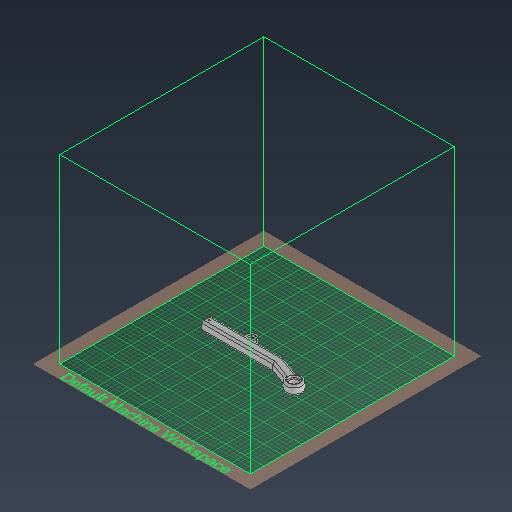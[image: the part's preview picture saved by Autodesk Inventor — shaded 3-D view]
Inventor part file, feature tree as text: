
AUTODESK INVENTOR PART (.ipt)
format: ipt  version: 2021 (Build 250183000, 183)  size: 555,520 bytes
history: native  units: mm
features: extrude x11, sketch x9, fillet x2, shell x1
ambient origin geometry x8: Origin, YZ Plane, XZ Plane, XY Plane, X Axis, Y Axis, Z Axis, Center Point
bodies: Volumenkörper1 (feature_tree)
feature tree (23):
  sketch  "Skizze1"  dims[d5=20.0mm d56=0.0mm]
  sketch  "Skizze4"  dims[d57=0.0mm d58=60.0mm]
  extrude  "Extrusion1"  TaperAngle=0.0deg  [1 undecoded]
  sketch  "Skizze13"  dims[d129=12.0mm d130=0.0mm d133=3.2mm]
  extrude  "Extrusion13"  Depth=60.0mm
  extrude  "Extrusion14"  Depth=20.0mm TaperAngle=0.0deg
  shell  "Wandung2"  Thickness=10.0mm
  extrude  "Extrusion11"  Depth=12.0mm
  extrude  "Extrusion12"  Depth=10.0mm TaperAngle=0.0deg
  extrude  "Extrusion15"  Depth=10.0mm
  fillet  "Rundung7"  Radius=10.0mm
  extrude  "Extrusion19"  Depth=50.0mm
  extrude  "Extrusion20"  Depth=10.0mm
  fillet  "Rundung8"  Radius=24.3mm
  extrude  "Extrusion21"  Depth=20.0mm TaperAngle=0.0deg
  extrude  "Extrusion22"  Depth=20.0mm TaperAngle=0.0deg
  extrude  "Extrusion23"  Depth=2.6mm
  sketch  "Skizze12"  dims[d74=20.0mm d75=20.0mm d78=10.0mm d79=20.0mm d80=0.0mm d116=10.0mm]
  sketch  "Skizze14"  dims[d135=6.0mm d136=10.0mm d137=0.0mm]
  sketch  "Skizze17"  dims[d138=160.0mm d140=3.490659mm d141=10.0mm]
  sketch  "Skizze18"  dims[d142=110.0mm d143=50.0mm]
  sketch  "Skizze19"  dims[d144=10.0mm d147=10.0mm d148=24.3mm]
  sketch  "Skizze20"  dims[d149=34.0mm d150=20.0mm d151=0.0mm d152=20.0mm d153=0.0mm d154=2.6mm d155=4.0mm d157=18.0mm d158=10.0mm d159=0.0mm d160=10.0mm d161=10.0mm d162=20.0mm d167=10.0mm d176=12.0mm d177=12.0mm d178=6.0mm d179=12.0mm d180=12.0mm d181=6.0mm d182=3.0mm d183=0.0mm d184=12.0mm d185=12.0mm d186=6.0mm d187=3.0mm d188=0.0mm d189=2.0mm d190=10.0mm d191=0.0mm d192=7.0mm d193=10.0mm d194=10.0mm d195=3.0mm d196=0.0mm d197=3.2mm d198=3.0mm d199=0.0mm d81=0.5mm d82=0.872665mm d83=0.5mm d84=0.872665mm]
note: 1 required parameter value undecoded (feature->parameter linkage not recoverable at this tier; creation-order binding heuristic only, values carry confidence <= 0.55)
